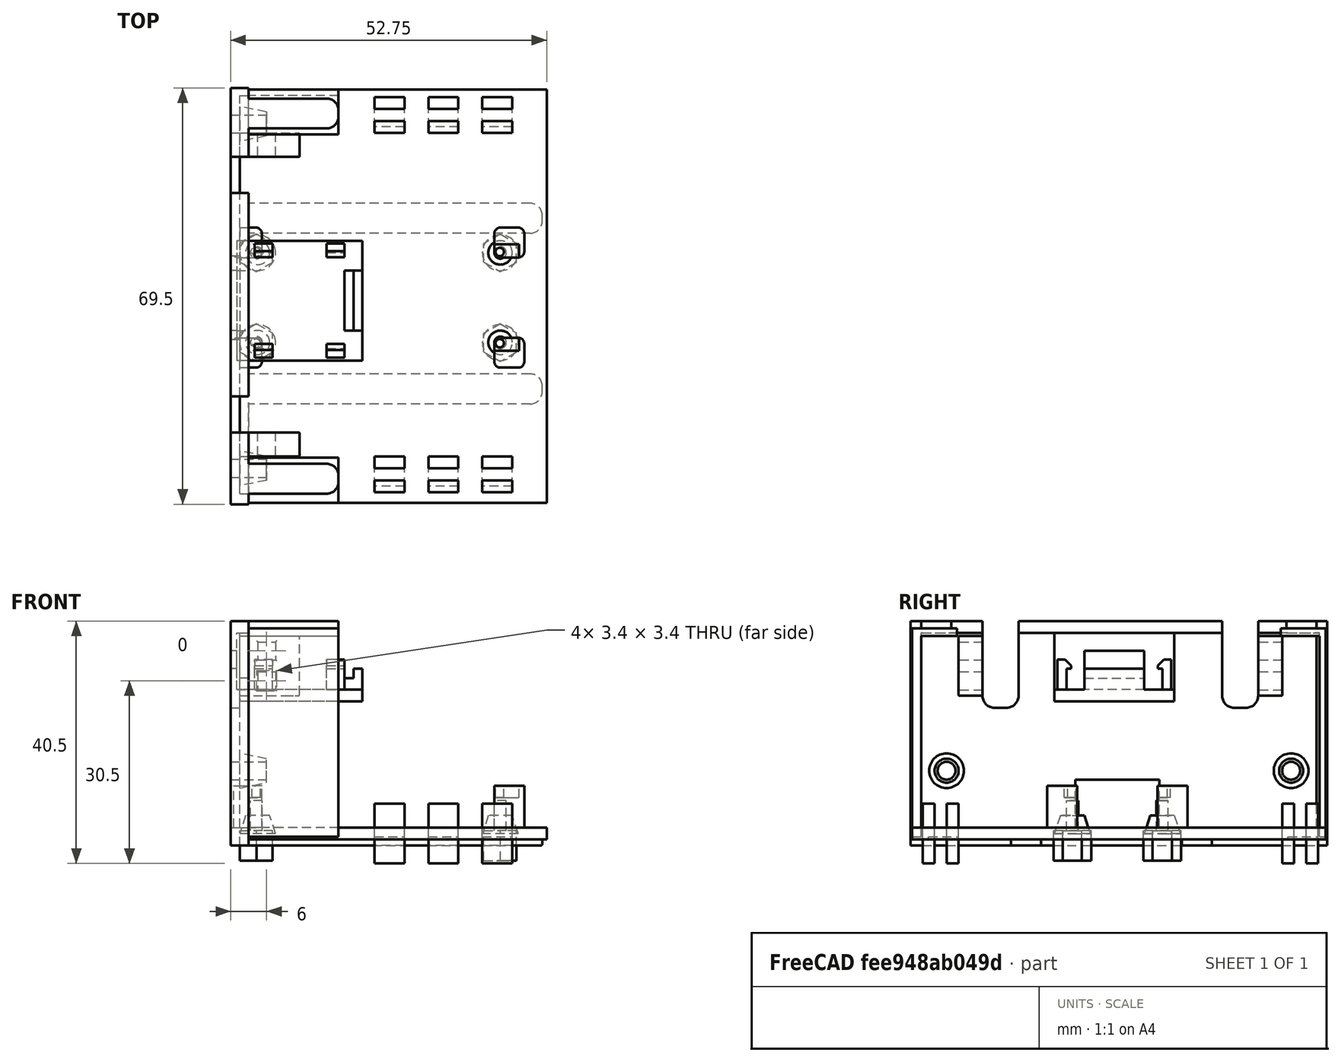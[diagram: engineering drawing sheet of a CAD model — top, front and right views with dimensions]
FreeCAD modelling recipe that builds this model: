
FCSTD DOCUMENT  (FreeCAD 0.19R24291 (Git))
Label: Arduino_Nano_33_BLE_tray_alt
License: All rights reserved
LicenseURL: http://en.wikipedia.org/wiki/All_rights_reserved
objects: Part::Box×80, Part::MultiFuse×37, Part::Fillet×18, Part::Cut×17, Part::Cylinder×10, Part::Cone×6, Part::MultiCommon×4, Part::Chamfer×2
note: 174 computed .brp shape members not serialized (recipe doc carries the construction recipe); baked Part::Feature solids carry a one-line shape summary decoded from their .brp

FEATURE [Part::Box] Box  label="Board"
  AttacherType = Attacher::AttachEngine3D
  Height = 10
  Length = 45.16
  Width = 17.76
FEATURE [Part::Cylinder] Cylinder
  Angle = 360
  AttacherType = Attacher::AttachEngine3D
  Height = 10
  Placement = pos=(1.26,1.26,0) rot=(0,0,1;0rad)
  Radius = 0.7
FEATURE [Part::Cylinder] Cylinder001
  Angle = 360
  AttacherType = Attacher::AttachEngine3D
  Height = 10
  Placement = pos=(41.9,1.26,0) rot=(0,0,1;0rad)
  Radius = 0.7
FEATURE [Part::Cylinder] Cylinder002
  Angle = 360
  AttacherType = Attacher::AttachEngine3D
  Height = 10
  Placement = pos=(1.26,16.5,0) rot=(0,0,1;0rad)
  Radius = 0.7
FEATURE [Part::Cylinder] Cylinder003
  Angle = 360
  AttacherType = Attacher::AttachEngine3D
  Height = 10
  Placement = pos=(41.9,16.5,0) rot=(0,0,1;0rad)
  Radius = 0.7
FEATURE [Part::MultiFuse] Fusion  label="Holes"
  Shapes = -> [Cylinder,Cylinder001,Cylinder002,Cylinder003]
FEATURE [Part::Cut] Cut  label="Arduino_board_shape"
  Base = -> Box
  Placement = pos=(0,25.62,3) rot=(0,0,1;0rad)
  Tool = -> Fusion
FEATURE [Part::Box] Box001  label="Cube"
  AttacherType = Attacher::AttachEngine3D
  Height = 37.5
  Length = 3
  Placement = pos=(-3,0,0) rot=(0,0,1;0rad)
  Width = 69.5
FEATURE [Part::Box] Box002  label="Cube001"
  AttacherType = Attacher::AttachEngine3D
  Height = 2
  Length = 50
  Placement = pos=(-0.25,0.25,1) rot=(0,0,1;0rad)
  Width = 69
FEATURE [Part::Box] Box003  label="Cube002"
  AttacherType = Attacher::AttachEngine3D
  Height = 34.75
  Length = 15
  Placement = pos=(0,0,2) rot=(0,0,1;0rad)
  Width = 7.5
FEATURE [Part::Box] Box004  label="Cube003"
  AttacherType = Attacher::AttachEngine3D
  Height = 34.75
  Length = 15
  Placement = pos=(0,61.5,2) rot=(0,0,1;0rad)
  Width = 7.5
FEATURE [Part::Box] Box005  label="Cube004"
  AttacherType = Attacher::AttachEngine3D
  Height = 34
  Length = 15
  Placement = pos=(0,1.5,1) rot=(0,0,1;0rad)
  Width = 7.5
FEATURE [Part::Box] Box006  label="Cube005"
  AttacherType = Attacher::AttachEngine3D
  Height = 34
  Length = 15
  Placement = pos=(0,60,1) rot=(0,0,1;0rad)
  Width = 7.5
FEATURE [Part::MultiFuse] Fusion001
  Shapes = -> [Box006,Box005]
FEATURE [Part::MultiFuse] Fusion002
  Placement = pos=(0,0,-0.5) rot=(0,0,1;0rad)
  Shapes = -> [Box004,Box003]
FEATURE [Part::Cut] Cut001
  Base = -> Fusion002
  Placement = pos=(0,0.25,0) rot=(0,0,1;0rad)
  Tool = -> Fusion001
FEATURE [Part::Box] Box007  label="Cube006"
  AttacherType = Attacher::AttachEngine3D
  Height = 32.5
  Length = 3.5
  Placement = pos=(-1.5,1.75,3) rot=(0,0,1;0rad)
  Width = 66.5
FEATURE [Part::Cut] Cut002
  Base = -> Box001
  Tool = -> Box007
FEATURE [Part::Cylinder] Cylinder004
  Angle = 360
  AttacherType = Attacher::AttachEngine3D
  Height = 10
  Placement = pos=(-5,6,32.5) rot=(0,1,0;1.5708rad)
  Radius = 1.5
FEATURE [Part::Cylinder] Cylinder005
  Angle = 360
  AttacherType = Attacher::AttachEngine3D
  Height = 10
  Placement = pos=(-5,63.5,32.5) rot=(0,1,0;1.5708rad)
  Radius = 1.5
FEATURE [Part::MultiFuse] Fusion003
  Placement = pos=(0,0,-20) rot=(0,0,1;0rad)
  Shapes = -> [Cylinder004,Cylinder005]
FEATURE [Part::Box] Box008  label="Cube007"
  AttacherType = Attacher::AttachEngine3D
  Height = 8
  Length = 10
  Placement = pos=(-5,27.5,3) rot=(0,0,1;0rad)
  Width = 14
FEATURE [Part::Cone] Cone
  Angle = 360
  AttacherType = Attacher::AttachEngine3D
  Height = 5
  Placement = pos=(-1,6,32.5) rot=(0,1,0;1.5708rad)
  Radius1 = 3
  Radius2 = 2
FEATURE [Part::Cone] Cone001
  Angle = 360
  AttacherType = Attacher::AttachEngine3D
  Height = 5
  Placement = pos=(-1,63.5,32.5) rot=(0,1,0;1.5708rad)
  Radius1 = 3
  Radius2 = 2
FEATURE [Part::MultiFuse] Fusion004
  Placement = pos=(-1,0,-20) rot=(0,0,1;0rad)
  Shapes = -> [Cone,Cone001]
  expr: .Placement.Base.z = -20
FEATURE [Part::MultiFuse] Fusion005
  Shapes = -> [Cut002,Fusion004]
FEATURE [Part::Cut] Cut003
  Base = -> Fusion005
  Tool = -> Fusion003
FEATURE [Part::Cut] Cut004
  Base = -> Cut003
  Tool = -> Box008
FEATURE [Part::Cone] Cone002
  Angle = 360
  AttacherType = Attacher::AttachEngine3D
  Height = 3
  Placement = pos=(42,27,2) rot=(0,0,1;0rad)
  Radius1 = 3
  Radius2 = 2
FEATURE [Part::Box] Box014  label="Cube014"
  AttacherType = Attacher::AttachEngine3D
  Height = 5
  Length = 5.45
  Placement = pos=(3.25,0,0) rot=(0,0,1;0rad)
  Width = 10
FEATURE [Part::Box] Box015  label="Cube015"
  AttacherType = Attacher::AttachEngine3D
  Height = 5
  Length = 5.45
  Placement = pos=(11.5,4,0) rot=(0,0,1;2.0944rad)
  Width = 10
FEATURE [Part::Box] Box016  label="Cube016"
  AttacherType = Attacher::AttachEngine3D
  Height = 5
  Length = 10
  Placement = pos=(0.55,4,0) rot=(0,0,-1;0.523599rad)
  Width = 5.45
FEATURE [Part::Cylinder] Cylinder006
  Angle = 360
  AttacherType = Attacher::AttachEngine3D
  Height = 10
  Placement = pos=(4,4,-1) rot=(0,0,1;0rad)
  Radius = 1
FEATURE [Part::MultiCommon] Common  label="M.25 nut"
  Placement = pos=(-2,0,-1) rot=(0,0,1;0rad)
  Shapes = -> [Box014,Box016,Box015]
FEATURE [Part::MultiFuse] Fusion008  label="screw_hole"
  Placement = pos=(-2.7,23,0) rot=(0,0,1;0rad)
  Shapes = -> [Cylinder006,Common]
FEATURE [Part::Cone] Cone003
  Angle = 360
  AttacherType = Attacher::AttachEngine3D
  Height = 3
  Placement = pos=(42,42,2) rot=(0,0,1;0rad)
  Radius1 = 3
  Radius2 = 2
FEATURE [Part::Cone] Cone004
  Angle = 360
  AttacherType = Attacher::AttachEngine3D
  Height = 3
  Placement = pos=(1.5,42,2) rot=(0,0,1;0rad)
  Radius1 = 3
  Radius2 = 2
FEATURE [Part::Cone] Cone005
  Angle = 360
  AttacherType = Attacher::AttachEngine3D
  Height = 3
  Placement = pos=(1.5,27,2) rot=(0,0,1;0rad)
  Radius1 = 3
  Radius2 = 2
FEATURE [Part::Box] Box017  label="Cube017"
  AttacherType = Attacher::AttachEngine3D
  Height = 5
  Length = 5.45
  Placement = pos=(3.25,0,0) rot=(0,0,1;0rad)
  Width = 10
FEATURE [Part::Box] Box018  label="Cube018"
  AttacherType = Attacher::AttachEngine3D
  Height = 5
  Length = 5.45
  Placement = pos=(11.5,4,0) rot=(0,0,1;2.0944rad)
  Width = 10
FEATURE [Part::Cylinder] Cylinder007
  Angle = 360
  AttacherType = Attacher::AttachEngine3D
  Height = 10
  Placement = pos=(4,4,-1) rot=(0,0,1;0rad)
  Radius = 1
FEATURE [Part::Box] Box019  label="Cube019"
  AttacherType = Attacher::AttachEngine3D
  Height = 5
  Length = 10
  Placement = pos=(0.55,4,0) rot=(0,0,-1;0.523599rad)
  Width = 5.45
FEATURE [Part::MultiCommon] Common001  label="M.25 nut001"
  Placement = pos=(-2,0,-1) rot=(0,0,1;0rad)
  Shapes = -> [Box017,Box019,Box018]
FEATURE [Part::MultiFuse] Fusion009  label="screw_hole001"
  Placement = pos=(-2.7,38,0) rot=(0,0,1;0rad)
  Shapes = -> [Cylinder007,Common001]
FEATURE [Part::Box] Box020  label="Cube020"
  AttacherType = Attacher::AttachEngine3D
  Height = 5
  Length = 5.45
  Placement = pos=(3.25,0,0) rot=(0,0,1;0rad)
  Width = 10
FEATURE [Part::Box] Box021  label="Cube021"
  AttacherType = Attacher::AttachEngine3D
  Height = 5
  Length = 5.45
  Placement = pos=(11.5,4,0) rot=(0,0,1;2.0944rad)
  Width = 10
FEATURE [Part::Cylinder] Cylinder008
  Angle = 360
  AttacherType = Attacher::AttachEngine3D
  Height = 10
  Placement = pos=(4,4,-1) rot=(0,0,1;0rad)
  Radius = 1
FEATURE [Part::Box] Box022  label="Cube022"
  AttacherType = Attacher::AttachEngine3D
  Height = 5
  Length = 10
  Placement = pos=(0.55,4,0) rot=(0,0,-1;0.523599rad)
  Width = 5.45
FEATURE [Part::MultiCommon] Common002  label="M.25 nut002"
  Placement = pos=(-2,0,-1) rot=(0,0,1;0rad)
  Shapes = -> [Box020,Box022,Box021]
FEATURE [Part::MultiFuse] Fusion010  label="screw_hole002"
  Placement = pos=(38,23,0) rot=(0,0,1;0rad)
  Shapes = -> [Cylinder008,Common002]
FEATURE [Part::Box] Box023  label="Cube023"
  AttacherType = Attacher::AttachEngine3D
  Height = 5
  Length = 5.45
  Placement = pos=(3.25,0,0) rot=(0,0,1;0rad)
  Width = 10
FEATURE [Part::Box] Box024  label="Cube024"
  AttacherType = Attacher::AttachEngine3D
  Height = 5
  Length = 5.45
  Placement = pos=(11.5,4,0) rot=(0,0,1;2.0944rad)
  Width = 10
FEATURE [Part::Cylinder] Cylinder009
  Angle = 360
  AttacherType = Attacher::AttachEngine3D
  Height = 10
  Placement = pos=(4,4,-1) rot=(0,0,1;0rad)
  Radius = 1
FEATURE [Part::Box] Box025  label="Cube025"
  AttacherType = Attacher::AttachEngine3D
  Height = 5
  Length = 10
  Placement = pos=(0.55,4,0) rot=(0,0,-1;0.523599rad)
  Width = 5.45
FEATURE [Part::MultiCommon] Common003  label="M.25 nut003"
  Placement = pos=(-2,0,-1) rot=(0,0,1;0rad)
  Shapes = -> [Box023,Box025,Box024]
FEATURE [Part::MultiFuse] Fusion011  label="screw_hole003"
  Placement = pos=(38,38,0) rot=(0,0,1;0rad)
  Shapes = -> [Cylinder009,Common003]
FEATURE [Part::MultiFuse] Fusion012  label="Screw holes cut"
  Placement = pos=(0,0,-1.5) rot=(0,0,1;0rad)
  Shapes = -> [Fusion008,Fusion009,Fusion010,Fusion011]
FEATURE [Part::MultiFuse] Fusion014
  Shapes = -> [Cut004,Box002]
FEATURE [Part::MultiFuse] Fusion015
  Shapes = -> [Cut001]
FEATURE [Part::Box] Box026  label="Cube026"
  AttacherType = Attacher::AttachEngine3D
  Height = 15
  Length = 10
  Placement = pos=(0,0,16) rot=(0,0,1;0rad)
  Width = 6
FEATURE [Part::Fillet] Fillet012
  Base = -> Box026
  Edges = 2 edges r=2: [Edge9,Edge11]
  Placement = pos=(-4,12,7) rot=(0,0,1;0rad)
FEATURE [Part::Box] Box027  label="Cube027"
  AttacherType = Attacher::AttachEngine3D
  Height = 15
  Length = 10
  Placement = pos=(0,0,16) rot=(0,0,1;0rad)
  Width = 6
FEATURE [Part::Fillet] Fillet013
  Base = -> Box027
  Edges = 2 edges r=2: [Edge9,Edge11]
  Placement = pos=(-4,52,7) rot=(0,0,1;0rad)
FEATURE [Part::MultiFuse] Fusion016  label="Cables sockets"
  Shapes = -> [Fillet012,Fillet013]
FEATURE [Part::Cut] Cut006  label="Arduino_Nano_33_BLE_tray"
  Base = -> Fusion015
  Tool = -> Fusion016
FEATURE [Part::Box] Box028  label="Cube028"
  AttacherType = Attacher::AttachEngine3D
  Height = 2
  Length = 15
  Placement = pos=(0,-15.5,0) rot=(0,0,1;0rad)
  Width = 5
FEATURE [Part::Fillet] Fillet
  Base = -> Box028
  Edges = 2 edges r=2: [Edge5,Edge7]
  Placement = pos=(0,17,0) rot=(0,0,1;0rad)
FEATURE [Part::Box] Box029  label="Cube029"
  AttacherType = Attacher::AttachEngine3D
  Height = 2
  Length = 49
  Width = 5
FEATURE [Part::Fillet] Fillet014
  Base = -> Box029
  Edges = 2 edges r=2: [Edge5,Edge7]
  Placement = pos=(0,45,0) rot=(0,0,1;0rad)
FEATURE [Part::Fillet] Fillet015
  Base = -> Fillet
  Edges = 2 edges r=0.25: [Edge14,Edge16]
  Placement = pos=(0,0.25,35.5) rot=(0,0,1;0rad)
FEATURE [Part::Fillet] Fillet016
  Base = -> Fillet014
  Edges = 2 edges r=0.25: [Edge14,Edge16]
  Placement = pos=(0,0.25,0) rot=(0,0,1;0rad)
FEATURE [Part::Box] Box030  label="Cube030"
  AttacherType = Attacher::AttachEngine3D
  Height = 2
  Length = 49
  Width = 5
FEATURE [Part::Fillet] Fillet017
  Base = -> Box030
  Edges = 2 edges r=2: [Edge5,Edge7]
  Placement = pos=(0,17,0) rot=(0,0,1;0rad)
FEATURE [Part::Fillet] Fillet018
  Base = -> Fillet017
  Edges = 2 edges r=0.25: [Edge14,Edge16]
  Placement = pos=(0,-0.25,0) rot=(0,0,1;0rad)
FEATURE [Part::Box] Box031  label="Cube031"
  AttacherType = Attacher::AttachEngine3D
  Height = 2
  Length = 15
  Placement = pos=(0,-15.25,0) rot=(0,0,1;0rad)
  Width = 5
FEATURE [Part::Fillet] Fillet019
  Base = -> Box031
  Edges = 2 edges r=2: [Edge5,Edge7]
  Placement = pos=(0,17,0) rot=(0,0,1;0rad)
FEATURE [Part::Fillet] Fillet020
  Base = -> Fillet019
  Edges = 2 edges r=0.25: [Edge14,Edge16]
  Placement = pos=(0,61,35.5) rot=(0,0,1;0rad)
FEATURE [Part::MultiFuse] Fusion017  label="rails"
  Shapes = -> [Fillet015,Fillet016,Fillet018,Fillet020]
FEATURE [Part::MultiFuse] Fusion018  label="Arduino tray rough"
  Shapes = -> [Cut006,Fusion017]
FEATURE [Part::Box] Box032  label="Cube032"
  AttacherType = Attacher::AttachEngine3D
  Height = 10
  Length = 10
  Placement = pos=(0,8,26) rot=(0,0,1;0rad)
  Width = 4
FEATURE [Part::Box] Box033  label="Cube033"
  AttacherType = Attacher::AttachEngine3D
  Height = 3
  Length = 3
  Placement = pos=(3,5,27) rot=(0,0,1;0rad)
  Width = 10
FEATURE [Part::Box] Box034  label="Cube034"
  AttacherType = Attacher::AttachEngine3D
  Height = 3
  Length = 3
  Placement = pos=(3,5,32) rot=(0,0,1;0rad)
  Width = 10
FEATURE [Part::MultiFuse] Fusion019
  Shapes = -> [Box033,Box034]
FEATURE [Part::Cut] Cut007
  Base = -> Box032
  Tool = -> Fusion019
FEATURE [Part::Fillet] Fillet022  label="zip ties holder"
  Base = -> Cut007
  Edges = 22 edges r=0.2: [Edge5,Edge6,Edge7,Edge8,Edge9,Edge10,Edge11,Edge12,Edge13,Edge14,Edge15,Edge16,Edge19,Edge20,Edge21,Edge22,Edge23,Edge24,Edge25,Edge26,Edge27,Edge28]
  Placement = pos=(-1,0,-1) rot=(0,0,1;0rad)
FEATURE [Part::Box] Box035  label="Cube035"
  AttacherType = Attacher::AttachEngine3D
  Height = 10
  Length = 10
  Placement = pos=(0,10,26) rot=(0,0,1;0rad)
  Width = 4
FEATURE [Part::Box] Box036  label="Cube036"
  AttacherType = Attacher::AttachEngine3D
  Height = 3
  Length = 3
  Placement = pos=(3,10,27) rot=(0,0,1;0rad)
  Width = 10
FEATURE [Part::Box] Box037  label="Cube037"
  AttacherType = Attacher::AttachEngine3D
  Height = 3
  Length = 3
  Placement = pos=(3,10,32) rot=(0,0,1;0rad)
  Width = 10
FEATURE [Part::MultiFuse] Fusion020
  Shapes = -> [Box036,Box037]
FEATURE [Part::Cut] Cut008
  Base = -> Box035
  Tool = -> Fusion020
FEATURE [Part::Fillet] Fillet023  label="zip ties holder001"
  Base = -> Cut008
  Edges = 22 edges r=0.2: [Edge5,Edge6,Edge7,Edge8,Edge9,Edge10,Edge11,Edge12,Edge13,Edge14,Edge15,Edge16,Edge19,Edge20,Edge21,Edge22,Edge23,Edge24,Edge25,Edge26,Edge27,Edge28]
  Placement = pos=(-1,48,-1) rot=(0,0,1;0rad)
FEATURE [Part::MultiFuse] Fusion021  label="zip ties holders"
  Placement = pos=(-0.5,0,0) rot=(0,0,1;0rad)
  Shapes = -> [Fillet022,Fillet023]
FEATURE [Part::Box] Box038  label="Cube038"
  AttacherType = Attacher::AttachEngine3D
  Height = 10
  Length = 5
  Placement = pos=(21,2,-3) rot=(0,0,1;0rad)
  Width = 2
FEATURE [Part::Box] Box039  label="Cube039"
  AttacherType = Attacher::AttachEngine3D
  Height = 10
  Length = 5
  Placement = pos=(30,2,-3) rot=(0,0,1;0rad)
  Width = 2
FEATURE [Part::Box] Box040  label="Cube040"
  AttacherType = Attacher::AttachEngine3D
  Height = 10
  Length = 5
  Placement = pos=(39,2,-3) rot=(0,0,1;0rad)
  Width = 2
FEATURE [Part::MultiFuse] Fusion022  label="zip ties holes board r"
  Shapes = -> [Box038,Box039,Box040]
FEATURE [Part::Box] Box041  label="Cube041"
  AttacherType = Attacher::AttachEngine3D
  Height = 10
  Length = 5
  Placement = pos=(21,2,-3) rot=(0,0,1;0rad)
  Width = 2
FEATURE [Part::Box] Box042  label="Cube042"
  AttacherType = Attacher::AttachEngine3D
  Height = 10
  Length = 5
  Placement = pos=(30,2,-3) rot=(0,0,1;0rad)
  Width = 2
FEATURE [Part::Box] Box043  label="Cube043"
  AttacherType = Attacher::AttachEngine3D
  Height = 10
  Length = 5
  Placement = pos=(39,2,-3) rot=(0,0,1;0rad)
  Width = 2
FEATURE [Part::MultiFuse] Fusion023  label="zip ties holes board l"
  Placement = pos=(0,64,0) rot=(0,0,1;0rad)
  Shapes = -> [Box041,Box042,Box043]
FEATURE [Part::Box] Box044  label="Cube044"
  AttacherType = Attacher::AttachEngine3D
  Height = 10
  Length = 5
  Placement = pos=(21,2,-3) rot=(0,0,1;0rad)
  Width = 2
FEATURE [Part::Box] Box045  label="Cube045"
  AttacherType = Attacher::AttachEngine3D
  Height = 10
  Length = 5
  Placement = pos=(30,2,-3) rot=(0,0,1;0rad)
  Width = 2
FEATURE [Part::Box] Box046  label="Cube046"
  AttacherType = Attacher::AttachEngine3D
  Height = 10
  Length = 5
  Placement = pos=(39,2,-3) rot=(0,0,1;0rad)
  Width = 2
FEATURE [Part::MultiFuse] Fusion024  label="zip ties holes board r001"
  Placement = pos=(0,4,0) rot=(0,0,1;0rad)
  Shapes = -> [Box044,Box045,Box046]
FEATURE [Part::Box] Box047  label="Cube047"
  AttacherType = Attacher::AttachEngine3D
  Height = 10
  Length = 5
  Placement = pos=(21,2,-3) rot=(0,0,1;0rad)
  Width = 2
FEATURE [Part::Box] Box048  label="Cube048"
  AttacherType = Attacher::AttachEngine3D
  Height = 10
  Length = 5
  Placement = pos=(30,2,-3) rot=(0,0,1;0rad)
  Width = 2
FEATURE [Part::Box] Box049  label="Cube049"
  AttacherType = Attacher::AttachEngine3D
  Height = 10
  Length = 5
  Placement = pos=(39,2,-3) rot=(0,0,1;0rad)
  Width = 2
FEATURE [Part::MultiFuse] Fusion025  label="zip ties holes board l001"
  Placement = pos=(0,60,0) rot=(0,0,1;0rad)
  Shapes = -> [Box047,Box048,Box049]
FEATURE [Part::MultiFuse] Fusion026  label="zip ties holes"
  Shapes = -> [Fusion022,Fusion023,Fusion024,Fusion025]
FEATURE [Part::MultiFuse] Fusion027  label="Arduino_tray"
  Shapes = -> [Fusion021]
FEATURE [Part::Box] Box050  label="Cube050"
  AttacherType = Attacher::AttachEngine3D
  Height = 1.5
  Length = 5
  Placement = pos=(21,3,0) rot=(0,0,1;0rad)
  Width = 5
FEATURE [Part::Box] Box051  label="Cube051"
  AttacherType = Attacher::AttachEngine3D
  Height = 1.5
  Length = 5
  Placement = pos=(30,3,0) rot=(0,0,1;0rad)
  Width = 5
FEATURE [Part::Box] Box052  label="Cube052"
  AttacherType = Attacher::AttachEngine3D
  Height = 1.5
  Length = 5
  Placement = pos=(39,3,0) rot=(0,0,1;0rad)
  Width = 5
FEATURE [Part::Box] Box053  label="Cube053"
  AttacherType = Attacher::AttachEngine3D
  Height = 1.5
  Length = 5
  Placement = pos=(39,63,0) rot=(0,0,1;0rad)
  Width = 5
FEATURE [Part::Box] Box054  label="Cube054"
  AttacherType = Attacher::AttachEngine3D
  Height = 1.5
  Length = 5
  Placement = pos=(30,63,0) rot=(0,0,1;0rad)
  Width = 5
FEATURE [Part::Box] Box055  label="Cube055"
  AttacherType = Attacher::AttachEngine3D
  Height = 1.5
  Length = 5
  Placement = pos=(21,63,0) rot=(0,0,1;0rad)
  Width = 5
FEATURE [Part::MultiFuse] Fusion028
  Shapes = -> [Box050,Box051,Box052,Box053,Box054,Box055]
FEATURE [Part::Cut] Cut010
  Base = -> Fusion027
  Tool = -> Fusion028
FEATURE [Part::Box] Box056  label="Cube056"
  AttacherType = Attacher::AttachEngine3D
  Height = 7
  Length = 5
  Placement = pos=(-2.8,22.8,-2) rot=(0,0,1;0rad)
  Width = 5
FEATURE [Part::Box] Box057  label="Cube057"
  AttacherType = Attacher::AttachEngine3D
  Height = 7
  Length = 5
  Placement = pos=(-2.8,41.2,-2) rot=(0,0,1;0rad)
  Width = 5
FEATURE [Part::Box] Box058  label="Cube058"
  AttacherType = Attacher::AttachEngine3D
  Height = 7
  Length = 5
  Placement = pos=(41,41.2,-2) rot=(0,0,1;0rad)
  Width = 5
FEATURE [Part::Box] Box059  label="Cube059"
  AttacherType = Attacher::AttachEngine3D
  Height = 7
  Length = 5
  Placement = pos=(41,22.8,-2) rot=(0,0,1;0rad)
  Width = 5
FEATURE [Part::Fillet] Fillet024
  Base = -> Box056
  Edges = 4 edges r=1: [Edge1,Edge3,Edge5,Edge7]
FEATURE [Part::Fillet] Fillet025
  Base = -> Box057
  Edges = 4 edges r=1: [Edge1,Edge3,Edge5,Edge7]
FEATURE [Part::Fillet] Fillet026
  Base = -> Box058
  Edges = 4 edges r=1: [Edge1,Edge3,Edge5,Edge7]
FEATURE [Part::Fillet] Fillet027
  Base = -> Box059
  Edges = 4 edges r=1: [Edge1,Edge3,Edge5,Edge7]
FEATURE [Part::MultiFuse] Fusion029
  Shapes = -> [Fillet024,Fillet025,Fillet026,Fillet027]
FEATURE [Part::Cut] Cut011
  Base = -> Fusion029
  Placement = pos=(0,0,5) rot=(0,0,1;0rad)
  Tool = -> Cut
FEATURE [Part::Box] Box060  label="Cube060"
  AttacherType = Attacher::AttachEngine3D
  Height = 34.75
  Length = 15
  Placement = pos=(0,0,2) rot=(0,0,1;0rad)
  Width = 7.5
FEATURE [Part::Box] Box061  label="Cube061"
  AttacherType = Attacher::AttachEngine3D
  Height = 34.75
  Length = 15
  Placement = pos=(0,61.5,2) rot=(0,0,1;0rad)
  Width = 7.5
FEATURE [Part::Box] Box062  label="Cube062"
  AttacherType = Attacher::AttachEngine3D
  Height = 34
  Length = 15
  Placement = pos=(0,1.5,1) rot=(0,0,1;0rad)
  Width = 7.5
FEATURE [Part::Box] Box063  label="Cube063"
  AttacherType = Attacher::AttachEngine3D
  Height = 34
  Length = 15
  Placement = pos=(0,60.5,1) rot=(0,0,1;0rad)
  Width = 7.5
FEATURE [Part::MultiFuse] Fusion030
  Shapes = -> [Box063,Box062]
FEATURE [Part::MultiFuse] Fusion031
  Placement = pos=(0,0,-0.5) rot=(0,0,1;0rad)
  Shapes = -> [Box061,Box060]
FEATURE [Part::Cut] Cut012
  Base = -> Fusion031
  Placement = pos=(0,0.25,0) rot=(0,0,1;0rad)
  Tool = -> Fusion030
FEATURE [Part::Box] Box064  label="Cube064"
  AttacherType = Attacher::AttachEngine3D
  Height = 15
  Length = 10
  Placement = pos=(0,0,16) rot=(0,0,1;0rad)
  Width = 6
FEATURE [Part::Fillet] Fillet028
  Base = -> Box064
  Edges = 2 edges r=2: [Edge9,Edge11]
  Placement = pos=(-4,12,7) rot=(0,0,1;0rad)
FEATURE [Part::Box] Box065  label="Cube065"
  AttacherType = Attacher::AttachEngine3D
  Height = 15
  Length = 10
  Placement = pos=(0,0,16) rot=(0,0,1;0rad)
  Width = 6
FEATURE [Part::Fillet] Fillet029
  Base = -> Box065
  Edges = 2 edges r=2: [Edge9,Edge11]
  Placement = pos=(-4,52,7) rot=(0,0,1;0rad)
FEATURE [Part::MultiFuse] Fusion032  label="Cables sockets001"
  Shapes = -> [Fillet028,Fillet029]
FEATURE [Part::MultiFuse] Fusion033
  Shapes = -> [Fusion014,Fusion018,Cut010,Cut011]
FEATURE [Part::Box] Box066  label="Cube066"
  AttacherType = Attacher::AttachEngine3D
  Height = 1.5
  Length = 5
  Placement = pos=(21,3,0) rot=(0,0,1;0rad)
  Width = 5
FEATURE [Part::Box] Box067  label="Cube067"
  AttacherType = Attacher::AttachEngine3D
  Height = 1.5
  Length = 5
  Placement = pos=(30,3,0) rot=(0,0,1;0rad)
  Width = 5
FEATURE [Part::Box] Box068  label="Cube068"
  AttacherType = Attacher::AttachEngine3D
  Height = 1.5
  Length = 5
  Placement = pos=(39,3,0) rot=(0,0,1;0rad)
  Width = 5
FEATURE [Part::Box] Box069  label="Cube069"
  AttacherType = Attacher::AttachEngine3D
  Height = 1.5
  Length = 5
  Placement = pos=(39,63,0) rot=(0,0,1;0rad)
  Width = 5
FEATURE [Part::Box] Box070  label="Cube070"
  AttacherType = Attacher::AttachEngine3D
  Height = 1.5
  Length = 5
  Placement = pos=(30,63,0) rot=(0,0,1;0rad)
  Width = 5
FEATURE [Part::Box] Box071  label="Cube071"
  AttacherType = Attacher::AttachEngine3D
  Height = 1.5
  Length = 5
  Placement = pos=(21,63,0) rot=(0,0,1;0rad)
  Width = 5
FEATURE [Part::MultiFuse] Fusion034
  Shapes = -> [Box066,Box067,Box068,Box069,Box070,Box071]
FEATURE [Part::MultiFuse] Fusion035
  Shapes = -> [Fusion034,Fusion032]
FEATURE [Part::Cut] Cut013
  Base = -> Fusion033
  Tool = -> Fusion035
FEATURE [Part::Box] Box072  label="Cube072"
  AttacherType = Attacher::AttachEngine3D
  Height = 5.5
  Length = 3
  Placement = pos=(16,3,-3.5) rot=(0,0,1;0rad)
  Width = 10
  expr: .Placement.Base.z = -3.5
FEATURE [Part::Box] Box073  label="Cube073"
  AttacherType = Attacher::AttachEngine3D
  Height = 10
  Length = 3
  Placement = pos=(0,0.75,-3) rot=(0,0,1;0rad)
  Width = 14.5
FEATURE [Part::Box] Box074  label="Cube074"
  AttacherType = Attacher::AttachEngine3D
  Height = 12
  Length = 1
  Placement = pos=(18,-2,-3.5) rot=(0,0,1;0rad)
  Width = 20
FEATURE [Part::Box] Box075  label="Cube075"
  AttacherType = Attacher::AttachEngine3D
  Height = 7
  Length = 3
  Placement = pos=(0,-1.5,-3.5) rot=(0,0,1;0rad)
  Width = 19
FEATURE [Part::Box] Box076  label="Cube076"
  AttacherType = Attacher::AttachEngine3D
  Height = 7
  Length = 3
  Placement = pos=(0,0,-5) rot=(0,0,1;0rad)
  Width = 16
FEATURE [Part::Box] Box077  label="Cube077"
  AttacherType = Attacher::AttachEngine3D
  Height = 10
  Length = 3
  Placement = pos=(0,0.75,-3) rot=(0,0,1;0rad)
  Width = 14.5
FEATURE [Part::MultiFuse] Fusion037
  Shapes = -> [Box076,Box077]
FEATURE [Part::Box] Box078  label="Cube078"
  AttacherType = Attacher::AttachEngine3D
  Height = 7
  Length = 3
  Placement = pos=(0,-1.5,-3.5) rot=(0,0,1;0rad)
  Width = 19
FEATURE [Part::Cut] Cut015
  Base = -> Box078
  Tool = -> Fusion037
FEATURE [Part::Chamfer] Chamfer001
  Base = -> Cut015
  Edges = 2 edges r=1: [Edge7,Edge27]
  Placement = pos=(12,0,0) rot=(0,0,1;0rad)
FEATURE [Part::Box] Box079  label="Cube079"
  AttacherType = Attacher::AttachEngine3D
  Height = 3
  Length = 2
  Placement = pos=(18,3,2) rot=(0,0,1;0rad)
  Width = 10
FEATURE [Part::Cut] Cut014
  Base = -> Box074
  Tool = -> Box079
FEATURE [Part::Box] Box080  label="Cube080"
  AttacherType = Attacher::AttachEngine3D
  Height = 7
  Length = 3
  Placement = pos=(0,0,-5) rot=(0,0,1;0rad)
  Width = 16
FEATURE [Part::MultiFuse] Fusion036
  Shapes = -> [Box080,Box073]
FEATURE [Part::Box] Box081  label="ttl-usb-board"
  AttacherType = Attacher::AttachEngine3D
  Height = 1.6
  Length = 19.5
  Placement = pos=(-1.5,0,0.4) rot=(0,0,1;0rad)
  Width = 16
FEATURE [Part::Cut] Cut016
  Base = -> Box075
  Tool = -> Fusion036
FEATURE [Part::Chamfer] Chamfer
  Base = -> Cut016
  Edges = 2 edges r=1: [Edge7,Edge27]
FEATURE [Part::Box] Box082  label="Cube081"
  AttacherType = Attacher::AttachEngine3D
  Height = 5.5
  Length = 3
  Placement = pos=(-3,3,-3.5) rot=(0,0,1;0rad)
  Width = 10
  expr: .Placement.Base.z = -3.5
FEATURE [Part::Box] Box083  label="Cube082"
  AttacherType = Attacher::AttachEngine3D
  Height = 2
  Length = 21
  Placement = pos=(-3,-2,-3.5) rot=(0,0,1;0rad)
  Width = 20
FEATURE [Part::MultiFuse] Fusion007
  Shapes = -> [Box082,Box083,Chamfer,Cut014,Box072,Chamfer001]
FEATURE [Part::Cut] Cut005  label="ttl-usb-ver2"
  Base = -> Fusion007
  Placement = pos=(16,42,27.55) rot=(0,0,1;3.14159rad)
  Tool = -> Box081
FEATURE [Part::Box] Box084  label="Cube083"
  AttacherType = Attacher::AttachEngine3D
  Height = 11
  Length = 5
  Placement = pos=(-4,24,24.5) rot=(0,0,1;0rad)
  Width = 20
FEATURE [Part::Cut] Cut017
  Base = -> Cut013
  Tool = -> Box084
FEATURE [Part::MultiFuse] Fusion038  label="all"
  Shapes = -> [Cut017,Cut005]
